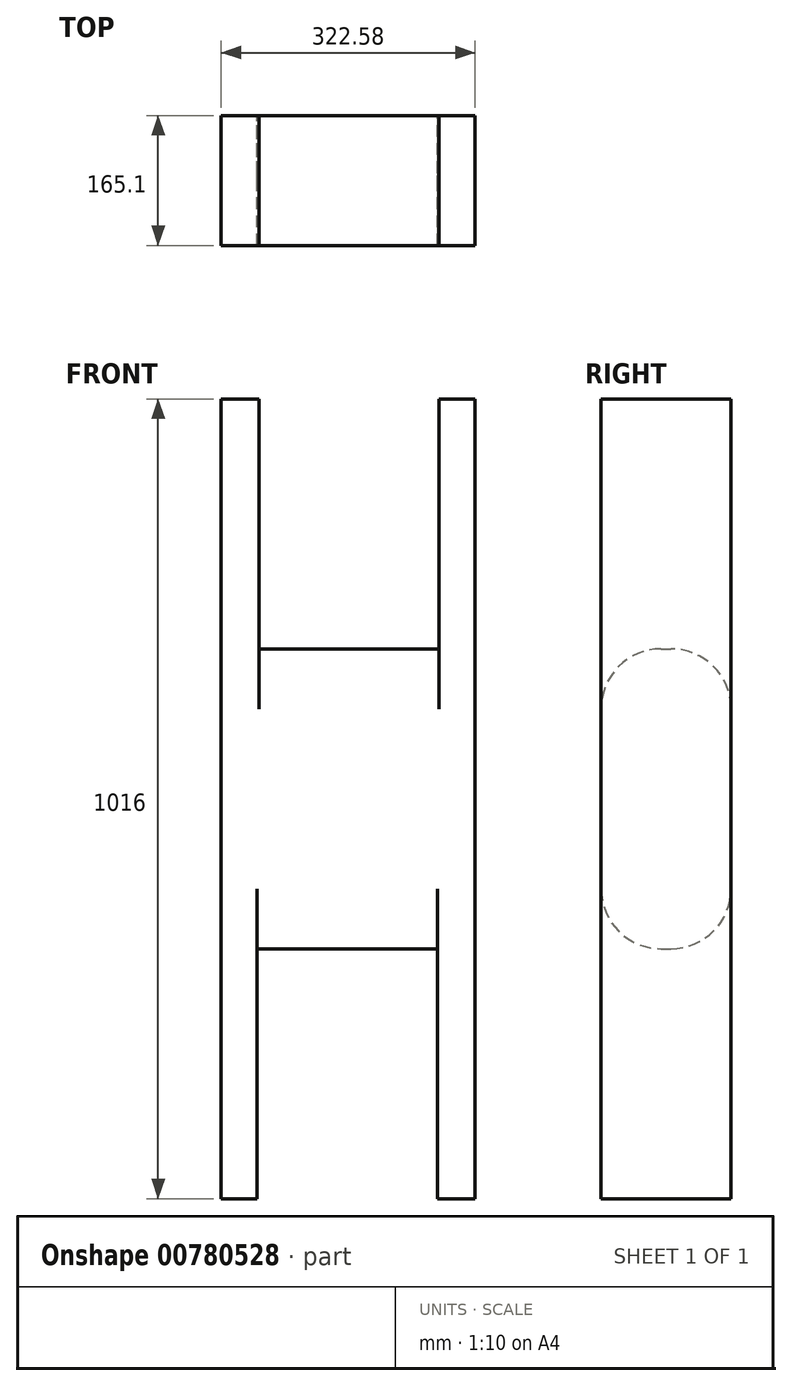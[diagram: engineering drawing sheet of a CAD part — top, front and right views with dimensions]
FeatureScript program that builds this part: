
annotation { "Feature Type Name" : "Feature", "Feature Type Description" : "" }
export const myFeature = defineFeature(function(context is Context, id is Id, definition is map)
    precondition{}
    {
        {
            var Q0;
            Q0=qCreatedBy(makeId("Front.planeOp"),FACE);
            var sketch = newSketch(context, id + "F0", { "sketchPlane" : qUnion([Q0])});
            skLineSegment(sketch, "E0.bottom", {"start": v(161.3, 508) * mm, "end": v(-161.29, 508) * mm});
            skLineSegment(sketch, "E0.top", {"start": v(161.3, -508) * mm, "end": v(-161.3, -508) * mm});
            skLineSegment(sketch, "E0.left", {"start": v(161.3, 508) * mm, "end": v(161.3, -508) * mm});
            skLineSegment(sketch, "E0.right", {"start": v(-161.29, 508) * mm, "end": v(-161.3, -508) * mm});
            skPoint(sketch, "E0.middle", {"position": v(0, 0) * mm});
            skLineSegment(sketch, "E1", {"start": v(0, 508) * mm, "end": v(0, 190.5) * mm});
            skLineSegment(sketch, "E2", {"start": v(0, 190.5) * mm, "end": v(115.4, 190.5) * mm});
            skLineSegment(sketch, "E3", {"start": v(115.4, 190.5) * mm, "end": v(115.4, 508) * mm});
            skLineSegment(sketch, "E4", {"start": v(115.4, 508) * mm, "end": v(-113.2, 508) * mm});
            skLineSegment(sketch, "E5", {"start": v(-113.2, 508) * mm, "end": v(-113.2, 190.5) * mm});
            skLineSegment(sketch, "E6", {"start": v(-113.2, 190.5) * mm, "end": v(0, 190.5) * mm});
            skLineSegment(sketch, "E7.1.0", {"start": v(113.2, -508) * mm, "end": v(113.2, -190.5) * mm});
            skLineSegment(sketch, "E7.1.1", {"start": v(113.2, -190.5) * mm, "end": v(0, -190.5) * mm});
            skLineSegment(sketch, "E7.1.2", {"start": v(0, -508) * mm, "end": v(0, -190.5) * mm});
            skLineSegment(sketch, "E7.1.3", {"start": v(0, -190.5) * mm, "end": v(-115.4, -190.5) * mm});
            skLineSegment(sketch, "E7.1.4", {"start": v(-115.4, -190.5) * mm, "end": v(-115.4, -508) * mm});
            skLineSegment(sketch, "E7.1.5", {"start": v(-115.4, -508) * mm, "end": v(113.2, -508) * mm});
            skSolve(sketch);
        }
        {
            var Q0;
            {var subQ2=sQuery(id+"F0.wireOp",EDGE,"E0.left");Q0=makeQuery(id+"F0.imprint","IMPRINT",FACE,{"disambiguationData":[TD([[makeQuery(id+"F0.imprint","IMPRINT",EDGE,{"derivedFrom":subQ2}),-1.0]])]});}
            extrude(context, id + "F1", {"entities" : qUnion([Q0]), "endBound" : BoundingType.SYMMETRIC, "depth" : 165.1 * mm, "offsetDistance" : 25.4 * mm});
        }
        {
            var Q0;
            Q0=makeQuery(id+"F1.opExtrude","CAP_EDGE",EDGE,{"disambiguationData":[OSD([sQuery(id+"F0.wireOp",EDGE,"E2"),sQuery(id+"F0.wireOp",EDGE,"E6")])],"isStart":false});
            var Q1;
            Q1=makeQuery(id+"F1.opExtrude","CAP_EDGE",EDGE,{"disambiguationData":[OSD([sQuery(id+"F0.wireOp",EDGE,"E2"),sQuery(id+"F0.wireOp",EDGE,"E6")])],"isStart":true});
            var Q2;
            Q2=makeQuery(id+"F1.opExtrude","CAP_EDGE",EDGE,{"disambiguationData":[OSD([sQuery(id+"F0.wireOp",EDGE,"E7.1.1"),sQuery(id+"F0.wireOp",EDGE,"E7.1.3")])],"isStart":true});
            var Q3;
            Q3=makeQuery(id+"F1.opExtrude","CAP_EDGE",EDGE,{"disambiguationData":[OSD([sQuery(id+"F0.wireOp",EDGE,"E7.1.1"),sQuery(id+"F0.wireOp",EDGE,"E7.1.3")])],"isStart":false});
            fillet(context, id + "F2", {"entities" : qUnion([Q0, Q1, Q2, Q3]), "radius" : 76.2 * mm, "tangentPropagation" : true, "allowEdgeOverflow" : false});
        }
    });
